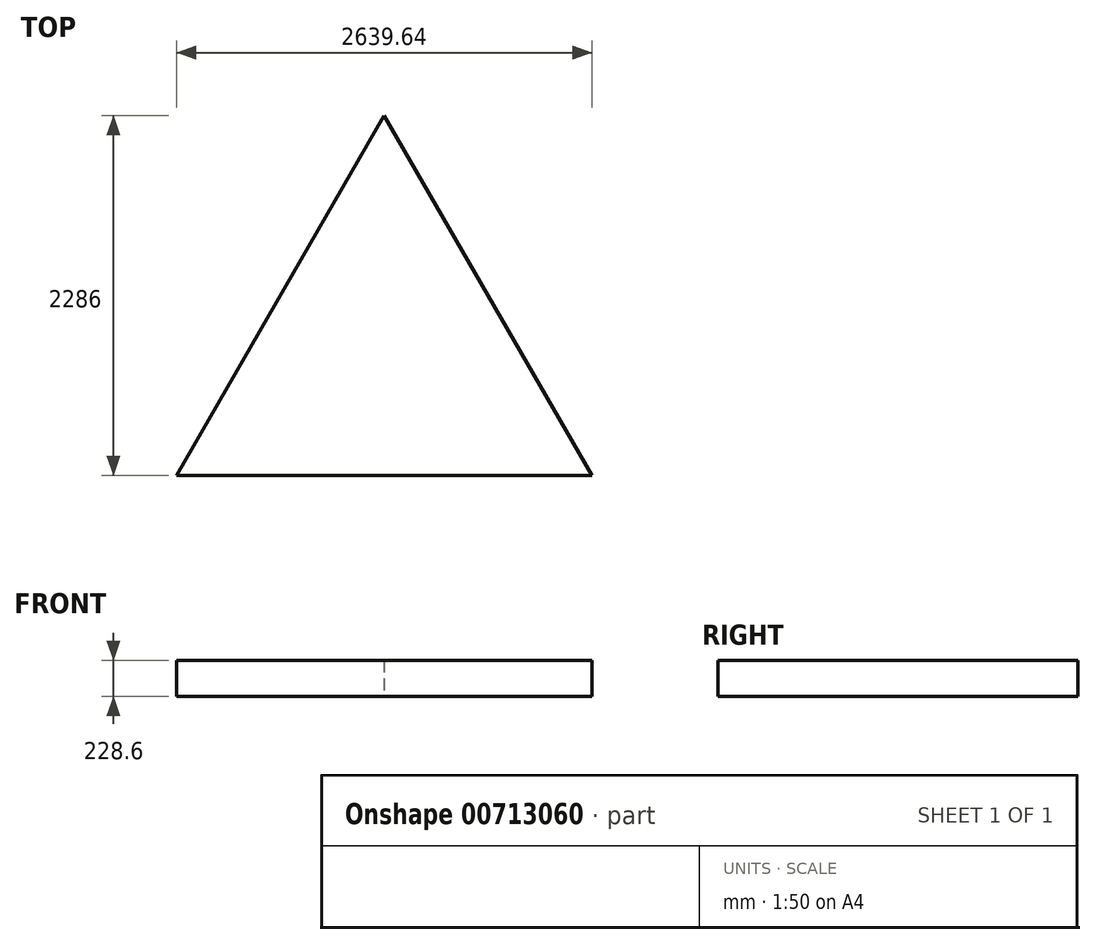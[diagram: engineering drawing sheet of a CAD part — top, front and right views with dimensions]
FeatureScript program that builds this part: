
annotation { "Feature Type Name" : "Feature", "Feature Type Description" : "" }
export const myFeature = defineFeature(function(context is Context, id is Id, definition is map)
    precondition{}
    {
        {
            var Q0;
            Q0=qCreatedBy(makeId("Top.planeOp"),FACE);
            var sketch = newSketch(context, id + "F0", { "sketchPlane" : qUnion([Q0])});
            skCircle(sketch, "E0", {"center": v(0, 0) * mm, "radius": 1397 * mm, "construction": true});
            skCircle(sketch, "E1", {"center": v(0, 0) * mm, "radius": 1270 * mm, "construction": true});
            skCircle(sketch, "E2", {"center": v(0, 0) * mm, "radius": 1524 * mm, "construction": true});
            skLineSegment(sketch, "E3", {"start": v(0, 1524) * mm, "end": v(-1319.82, -762) * mm});
            skLineSegment(sketch, "E4", {"start": v(-1319.82, -762) * mm, "end": v(1319.82, -762) * mm});
            skLineSegment(sketch, "E5", {"start": v(1319.82, -762) * mm, "end": v(0, 1524) * mm});
            skLineSegment(sketch, "E6", {"start": v(0, 0) * mm, "end": v(0, 879.92) * mm, "construction": true});
            skSolve(sketch);
        }
        {
            var Q0;
            Q0 = qSketchRegion(id + "F0", true);
            extrude(context, id + "F1", {"entities" : qUnion([Q0]), "depth" : 228.6 * mm, "offsetDistance" : 25.4 * mm});
        }
    });
